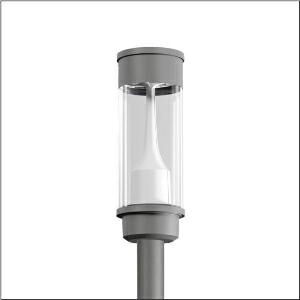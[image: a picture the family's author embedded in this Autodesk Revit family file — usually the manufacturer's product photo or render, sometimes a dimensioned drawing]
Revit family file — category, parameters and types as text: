
# Revit family: litepole_iq___pl1_2s_5xa5415jf14h_0c6a
name_source: partatom
category: Lighting Fixtures
units: mm (PartAtom-declared; Revit-internal decimal feet)

## family parameters
Cut with Voids When Loaded = No
Host = Face
Light Source = No
Part Type = Normal
Room Calculation Point = No
Round Connector Dimension = Use Diameter
Shared = No

## types (1)
- --- (1 x LED, 2970 lm, 19.3 W, 3000K)
    Apparent Load = 19 VA
    CIE Flux Codes = 23 62 94 96 100
    Color Rendering = 70
    Color Temperature = 3000K
    Default Elevation = 1800 mm
    Description = Litepole iQ, mast luminaire, Module 540 iQ-SR, primary light control with 3 zone facetted reflector, of plastic, silver coated, highly specular, structured, primary optical cover: cover, of PMMA, transparent, light distribution: PL1.2s, light emission: direct distribution, primary light characteristic: symmetric, installation type: post-top, LED, High Power LED, rated luminous flux: 2.970lm, luminous efficacy: 154lm/W, light colour: 730, colour temperature: 3000K, control gear: ECG iQ, control: Auto-Match, Temp-Guard, Lumen-Switch, Night-Set, Smart-Wire, Light-Fading, Desk-Remote (wireless, voltage-free reading and setting of iQ features in the workshop via application-optimized NFC function/RFID function), optimised constant luminous flux control (CLO 2.0), Street-Remote, presetting dimming logarithmic, with terminal, 6-pole, max. 2.5mm², mains connection: 230..240V, AC, 50/60Hz, start of lifetime: 19W, end of service life: 21W, reduction: 10W, luminaire housing, upper part, of glass-fibre reinforced polyester, coated, Siteco® metallic grey (DB 702S), diameter: 210mm, height: 590mm, spigot size: d x l = 76 x 70mm (post-top) | with reducer (optional accessory) 60 x 70mm, post-top mast mounting element, of diecast aluminium, coated, Siteco® metallic grey (DB 702S), Module 540 iQ-SR, traffic white (RAL 9016), equipment: standard, protection rating (complete): IP65, insulation class (complete): insulation class II (safety insulation), certification: CE, ENEC, VDE, packaging unit: 1 piece

Light Distribution: PL1.2s
    Height = 590 mm
    Lamp = 1 x LED
    Lamp Light Flux = 2970 lm
    Lamp Power = 19.3 W
    Lamp count = 1
    Length = 220 mm
    Luminous efficacy = 154 lm/W
    Manufacturer = Siteco
    ModVariant = No
    Model = 5XA5415JF14H
    Number of Poles = 1
    OnlyDefault = Yes
    Power Factor = 1
    Product Name = Litepole iQ | PL1.2s
    Product group = mast luminaire | pylon top
    ProductGroupID = 6100
    Protection Class = Protection class II
    Protection Degree = IP 65
    RLX_Detail_Level = 1
    RLX_Emergency_Light_Flux = 0 lm
    RLX_Emergency_Type = 0
    RLX_Emergency_Type_DB = No
    RlxData = <blob elided: 40377 chars, md5=1840bbaf>
    Socket = socket
    Standby Power = 0 W
    System Light Flux = 2970 lm
    System Power = 19 W
    Type Comments = factory setting: luminous flux: 100 % | dim-lin: 254 | 403 mA
    Type Image = l_1006025.jpg
    URL = http://relux.com
    VarID = @adj_094323
    Voltage = 0 V
    Weight = 0.00 kg
    Width = 0 mm  [stored 0 ft]

note: [stored X ft] marks values corroborated as IEEE doubles in the binary element streams (Revit-internal decimal feet)

## geometry (parser evidence)
native form markers: Blend x4, Sweep x10
no freeform markers — native parametric forms only
